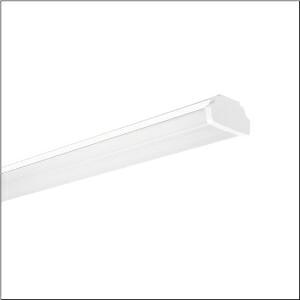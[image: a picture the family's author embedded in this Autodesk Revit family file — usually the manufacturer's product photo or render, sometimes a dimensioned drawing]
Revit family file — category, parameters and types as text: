
# Revit family: modario_r__31_gen_2_53bm812mv4fxd2_4edd
name_source: partatom
category: Lighting Fixtures
units: mm (PartAtom-declared; Revit-internal decimal feet)

## family parameters
Cut with Voids When Loaded = No
Host = Face
Light Source = No
Part Type = Normal
Room Calculation Point = No
Round Connector Dimension = Use Diameter
Shared = No

## types (1)
- --- (1 x LED, 15440 lm, 82.3 W, 4000K)
    Apparent Load = 82 VA
    CIE Flux Codes = 47 80 95 93 100
    Color Rendering = 80
    Color Temperature = 4000K
    Default Elevation = 1800 mm
    Description = Modario® 31 Gen.2, luminaire insert, of sheet steel, coil coated, white, length: 1.495mm, width: 81mm, height: 82mm, 5x system unit, system units: 299mm, LED rated luminous flux: 15.440lm, light colour: 840, control gear: ON/OFF Multilumen, control gear: ECG, with plug, 3-pole, with phase selection, mains connection: 220..240V, AC, 50/60Hz, rated input power: 82W, through-wiring accessed according to module size, primary optical cover: cover, of PMMA, light emission: direct distribution, primary light characteristic: symmetric, protection rating (complete): IP20, protection rating (LED compartment): IP50, insulation class (complete): insulation class I (protective earthing), certification: CE, ENEC, VDE, UKCA, impact resistance: IK03, permissible ambient temperature for indoor applications: -35..+35°C, corresponds to IFS (International Featured Standards) requirements for safety and quality in the food industry, reducing of maximum allowable ambient temperature of 5°C with ceiling mounting, IP40 when using the optional accessory 5TP9018, packaging unit: 1 piece
    Height = 92 mm
    Lamp = 1 x LED
    Lamp Light Flux = 15440 lm
    Lamp Power = 82.3 W
    Lamp count = 1
    Length = 1495 mm
    Luminous efficacy = 188 lm/W
    Manufacturer = Siteco
    ModVariant = No
    Model = 53BM812MV4FXD2
    Mounting Place = Ceiling
    Mounting Type = Pendant
    Number of Poles = 1
    OnlyDefault = Yes
    Power Factor = 1
    Product Name = Modario® 31 Gen.2
    Product group = luminaire insert
    ProductGroupID = 901
    Protection Class = Protection class I
    Protection Degree = IP 20
    RLX_Detail_Level = 1
    RLX_Emergency_Light_Flux = 0 lm
    RLX_Emergency_Type = 0
    RLX_Emergency_Type_DB = No
    RlxData = <blob elided: 39973 chars, md5=8ede6057>
    Socket = socket
    Standby Power = 0 W
    System Light Flux = 15440 lm
    System Power = 82 W
    Type Comments = factory setting: luminous flux: 100 % | (A | C | E) | 193 mA
    Type Image = l_1319597.jpg
    URL = http://relux.com
    VarID = @adj_010681
    Voltage = 0 V
    Weight = 0.00 kg
    Width = 81 mm

## geometry (parser evidence)
native form markers: Blend x4, Sweep x11
no freeform markers — native parametric forms only
